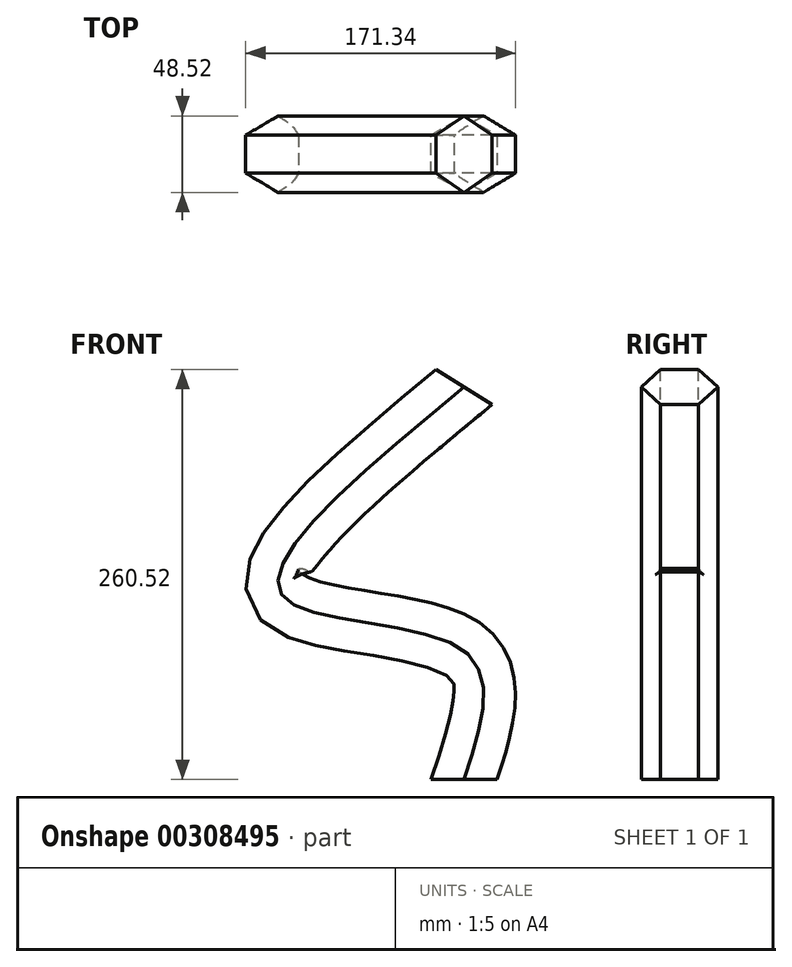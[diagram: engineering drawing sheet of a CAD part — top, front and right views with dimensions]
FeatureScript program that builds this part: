
annotation { "Feature Type Name" : "Feature", "Feature Type Description" : "" }
export const myFeature = defineFeature(function(context is Context, id is Id, definition is map)
    precondition{}
    {
        {
            var Q0;
            Q0=qCreatedBy(makeId("Top.planeOp"),FACE);
            var sketch = newSketch(context, id + "F0", { "sketchPlane" : qUnion([Q0])});
            skCircle(sketch, "E0.cCircle", {"center": v(0, 0) * mm, "radius": 21 * mm, "construction": true});
            skLineSegment(sketch, "E0.0", {"start": v(-21, -12.13) * mm, "end": v(-21, 12.13) * mm});
            skLineSegment(sketch, "E0.1", {"start": v(-21, 12.13) * mm, "end": v(0, 24.26) * mm});
            skLineSegment(sketch, "E0.2", {"start": v(0, 24.26) * mm, "end": v(21, 12.13) * mm});
            skLineSegment(sketch, "E0.3", {"start": v(21, 12.13) * mm, "end": v(21, -12.13) * mm});
            skLineSegment(sketch, "E0.4", {"start": v(21, -12.13) * mm, "end": v(0, -24.26) * mm});
            skLineSegment(sketch, "E0.5", {"start": v(0, -24.26) * mm, "end": v(-21, -12.13) * mm});
            skPoint(sketch, "E0.0.midPoint", {"position": v(-21, 0) * mm});
            skSolve(sketch);
        }
        {
            var Q0;
            Q0=qCreatedBy(makeId("Front.planeOp"),FACE);
            var sketch = newSketch(context, id + "F1", { "sketchPlane" : qUnion([Q0])});
            skFitSpline(sketch, "E1", {"points": [v(0, 0) * mm, v(0, 81.74) * mm, v(-115.1, 116.44) * mm, v(0, 249.33) * mm], "startDerivative": vector(118.9, 360.28) * mm, "endDerivative": vector(502.79, 415.6) * mm});
            skSolve(sketch);
        }
        {
            var Q0;
            Q0=makeQuery(id+"F0.imprint","IMPRINT",FACE,{"disambiguationData":[TD([[makeQuery(id+"F0.imprint","IMPRINT",EDGE,{"derivedFrom":sQuery(id+"F0.wireOp",EDGE,"E0.0")}),-1.0]])]});
            var Q1;
            Q1=sQuery(id+"F1.wireOp",EDGE,"E1");
            sweep(context, id + "F2", {"profiles" : qUnion([Q0]), "path" : qUnion([Q1])});
        }
    });
